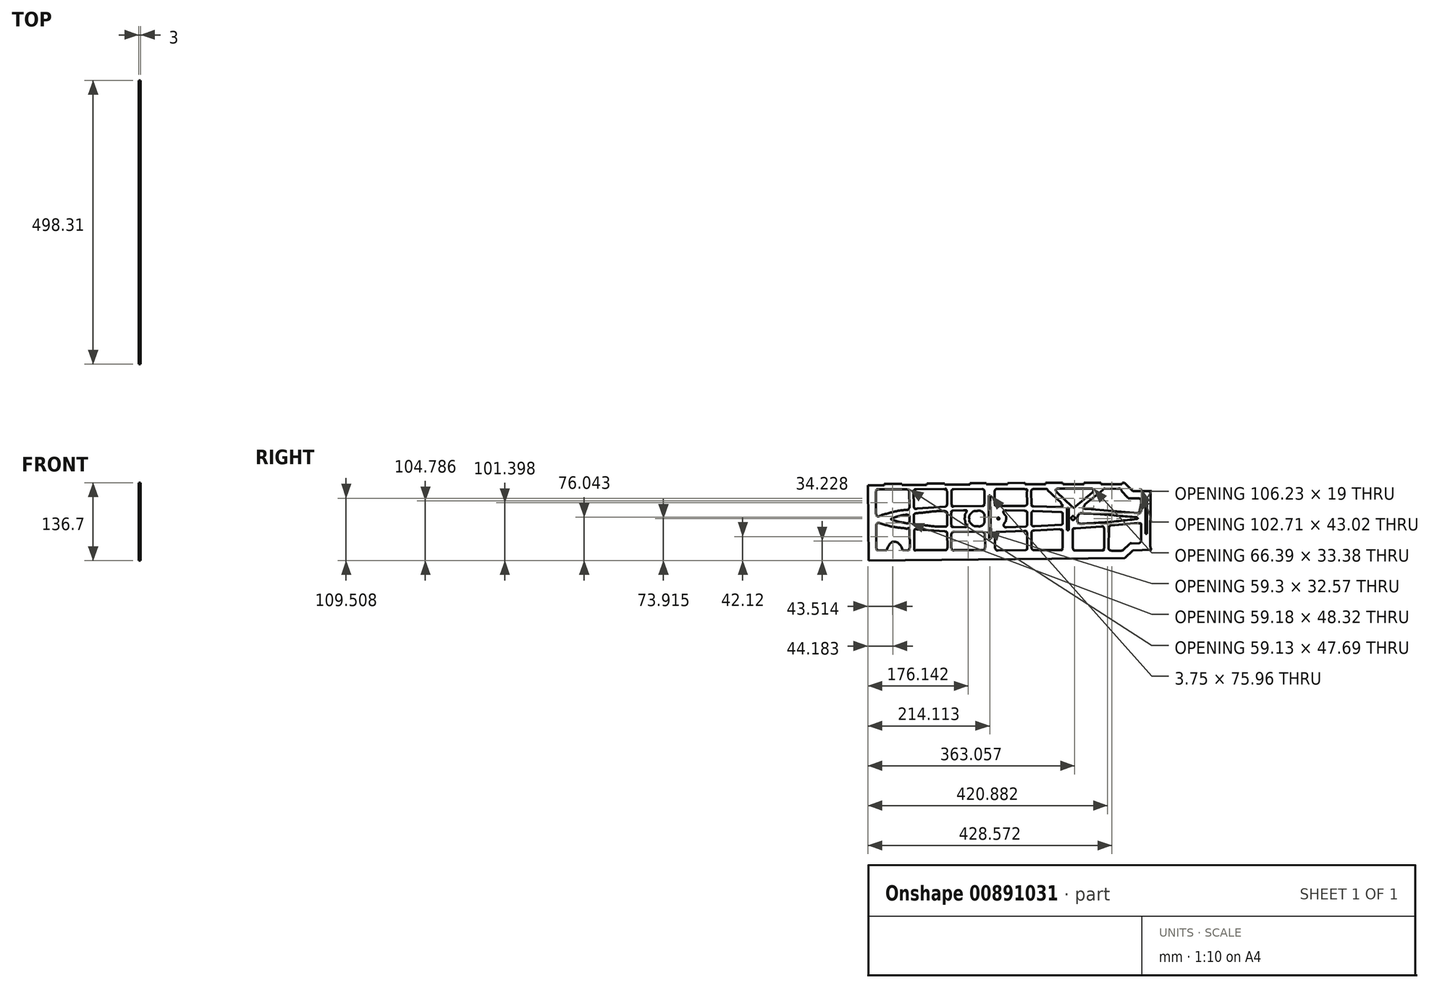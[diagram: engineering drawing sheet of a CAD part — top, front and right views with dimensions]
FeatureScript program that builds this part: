
annotation { "Feature Type Name" : "Feature", "Feature Type Description" : "" }
export const myFeature = defineFeature(function(context is Context, id is Id, definition is map)
    precondition{}
    {
        {
            var Q0;
            Q0=qCreatedBy(makeId("Right.planeOp"),FACE);
            var sketch = newSketch(context, id + "F0", { "sketchPlane" : qUnion([Q0])});
            skLineSegment(sketch, "E0", {"start": v(-252.36, 63.69) * mm, "end": v(-223.45, 63.69) * mm});
            skLineSegment(sketch, "E1", {"start": v(-223.45, 63.69) * mm, "end": v(-223.45, 66.35) * mm});
            skLineSegment(sketch, "E2", {"start": v(-223.45, 66.35) * mm, "end": v(-192.1, 66.21) * mm});
            skLineSegment(sketch, "E3", {"start": v(-192.1, 66.21) * mm, "end": v(-192.1, 64.1) * mm});
            skLineSegment(sketch, "E4", {"start": v(-192.1, 64.1) * mm, "end": v(-149.02, 64.53) * mm});
            skLineSegment(sketch, "E5", {"start": v(-149.02, 64.53) * mm, "end": v(-148.8, 66.91) * mm});
            skLineSegment(sketch, "E6", {"start": v(-148.8, 66.91) * mm, "end": v(-117.47, 67) * mm});
            skLineSegment(sketch, "E7", {"start": v(-117.47, 67) * mm, "end": v(-117.24, 64.87) * mm});
            skLineSegment(sketch, "E8", {"start": v(-117.24, 64.87) * mm, "end": v(-72.77, 65.07) * mm});
            skLineSegment(sketch, "E9", {"start": v(-72.77, 65.07) * mm, "end": v(-72.87, 67.27) * mm});
            skLineSegment(sketch, "E10", {"start": v(-72.87, 67.27) * mm, "end": v(-44.21, 67.47) * mm});
            skLineSegment(sketch, "E11", {"start": v(-44.21, 67.47) * mm, "end": v(-44.1, 65.43) * mm});
            skLineSegment(sketch, "E12", {"start": v(-44.1, 65.43) * mm, "end": v(-6.8, 65.66) * mm});
            skLineSegment(sketch, "E13", {"start": v(-6.8, 65.66) * mm, "end": v(-6.77, 67.67) * mm});
            skLineSegment(sketch, "E14", {"start": v(-6.77, 67.67) * mm, "end": v(23.4, 67.9) * mm});
            skLineSegment(sketch, "E15", {"start": v(23.4, 67.9) * mm, "end": v(23.47, 65.8) * mm});
            skLineSegment(sketch, "E16", {"start": v(23.47, 65.8) * mm, "end": v(59.52, 65.73) * mm});
            skLineSegment(sketch, "E17", {"start": v(59.52, 65.73) * mm, "end": v(59.8, 68.1) * mm});
            skLineSegment(sketch, "E18", {"start": v(59.8, 68.1) * mm, "end": v(89.83, 68.06) * mm});
            skLineSegment(sketch, "E19", {"start": v(89.83, 68.06) * mm, "end": v(90.13, 65.86) * mm});
            skLineSegment(sketch, "E20", {"start": v(90.13, 65.86) * mm, "end": v(126.94, 65.9) * mm});
            skLineSegment(sketch, "E21", {"start": v(126.94, 65.9) * mm, "end": v(126.8, 68.23) * mm});
            skLineSegment(sketch, "E22", {"start": v(126.8, 68.23) * mm, "end": v(156.97, 68.35) * mm});
            skLineSegment(sketch, "E23", {"start": v(156.97, 68.35) * mm, "end": v(157.08, 65.93) * mm});
            skLineSegment(sketch, "E24", {"start": v(157.08, 65.93) * mm, "end": v(193.78, 65.86) * mm});
            skLineSegment(sketch, "E25", {"start": v(193.78, 65.86) * mm, "end": v(194.06, 68.25) * mm});
            skLineSegment(sketch, "E26", {"start": v(194.06, 68.25) * mm, "end": v(198.27, 68.32) * mm});
            skLineSegment(sketch, "E27", {"start": v(198.27, 68.32) * mm, "end": v(212.86, 53.37) * mm});
            skLineSegment(sketch, "E28", {"start": v(212.86, 53.37) * mm, "end": v(252.36, 53.23) * mm});
            skLineSegment(sketch, "E29", {"start": v(243.66, 49.02) * mm, "end": v(243.52, -44.22) * mm});
            skLineSegment(sketch, "E30", {"start": v(250.68, -49) * mm, "end": v(212.95, -50.65) * mm});
            skLineSegment(sketch, "E31", {"start": v(212.95, -50.65) * mm, "end": v(198.74, -64.17) * mm});
            skLineSegment(sketch, "E32", {"start": v(198.74, -64.17) * mm, "end": v(-250.82, -68.35) * mm});
            skLineSegment(sketch, "E33", {"start": v(-250.82, -68.35) * mm, "end": v(-252.36, 63.69) * mm});
            skLineSegment(sketch, "E34", {"start": v(-234.1, 56.45) * mm, "end": v(-184.15, 56.9) * mm});
            skLineSegment(sketch, "E35", {"start": v(-179.86, 53.38) * mm, "end": v(-179.28, 24.52) * mm});
            skLineSegment(sketch, "E36", {"start": v(-237.93, 13.87) * mm, "end": v(-238.4, 52.2) * mm});
            skLineSegment(sketch, "E37", {"start": v(-166.84, 56.6) * mm, "end": v(-118.57, 57.23) * mm});
            skLineSegment(sketch, "E38", {"start": v(-113.3, 52.74) * mm, "end": v(-113.1, 30.64) * mm});
            skLineSegment(sketch, "E39", {"start": v(-116.53, 26.36) * mm, "end": v(-165.85, 22.78) * mm});
            skLineSegment(sketch, "E40", {"start": v(-171.68, 26.92) * mm, "end": v(-171.82, 52.95) * mm});
            skLineSegment(sketch, "E41", {"start": v(-101.8, 56.84) * mm, "end": v(-51.43, 57.37) * mm});
            skLineSegment(sketch, "E42", {"start": v(-47.85, 53.48) * mm, "end": v(-47.5, 32.96) * mm});
            skLineSegment(sketch, "E43", {"start": v(-51.44, 27.82) * mm, "end": v(-100.82, 27.06) * mm});
            skLineSegment(sketch, "E44", {"start": v(-105.59, 30.43) * mm, "end": v(-105.49, 53.35) * mm});
            skLineSegment(sketch, "E45", {"start": v(-179.21, 8.74) * mm, "end": v(-179.25, 0.2) * mm});
            skLineSegment(sketch, "E46", {"start": v(-206.6, 6.97) * mm, "end": v(-206.6, 6.97) * mm});
            skLineSegment(sketch, "E47", {"start": v(-178.97, -16.66) * mm, "end": v(-178.59, -45.67) * mm});
            skLineSegment(sketch, "E48", {"start": v(-181.9, -50.3) * mm, "end": v(-190.97, -50.13) * mm});
            skLineSegment(sketch, "E49", {"start": v(-219.62, -50.4) * mm, "end": v(-234.27, -50.26) * mm});
            skLineSegment(sketch, "E50", {"start": v(-237.35, -46.6) * mm, "end": v(-237.77, -6.6) * mm});
            skLineSegment(sketch, "E51", {"start": v(-113.1, 13.52) * mm, "end": v(-112.74, -4.65) * mm});
            skLineSegment(sketch, "E52", {"start": v(-171.26, -1.9) * mm, "end": v(-171.45, 10.26) * mm});
            skLineSegment(sketch, "E53", {"start": v(-103.04, 19.15) * mm, "end": v(-84.5, 19.9) * mm});
            skLineSegment(sketch, "E54", {"start": v(-80.9, -9.98) * mm, "end": v(-101.8, -9.35) * mm});
            skLineSegment(sketch, "E55", {"start": v(-105.7, -5.18) * mm, "end": v(-105.86, 15.1) * mm});
            skLineSegment(sketch, "E56", {"start": v(-165.01, -13.9) * mm, "end": v(-117.16, -17) * mm});
            skLineSegment(sketch, "E57", {"start": v(-112.88, -20.43) * mm, "end": v(-112.53, -45.34) * mm});
            skLineSegment(sketch, "E58", {"start": v(-116.88, -49.97) * mm, "end": v(-166.63, -49.97) * mm});
            skLineSegment(sketch, "E59", {"start": v(-170.9, -45.76) * mm, "end": v(-171.05, -18.47) * mm});
            skLineSegment(sketch, "E60", {"start": v(-101.1, -17.84) * mm, "end": v(-50.65, -18.33) * mm});
            skLineSegment(sketch, "E61", {"start": v(-46.7, -22.03) * mm, "end": v(-46.57, -44.97) * mm});
            skLineSegment(sketch, "E62", {"start": v(-50.85, -50.16) * mm, "end": v(-99.7, -49.83) * mm});
            skLineSegment(sketch, "E63", {"start": v(-105.87, -45.34) * mm, "end": v(-105.8, -22.96) * mm});
            skLineSegment(sketch, "E64", {"start": v(-40.12, 45.64) * mm, "end": v(-37.2, 45.67) * mm});
            skLineSegment(sketch, "E65", {"start": v(-37.2, 45.67) * mm, "end": v(-36.37, -30.25) * mm});
            skLineSegment(sketch, "E66", {"start": v(-36.37, -30.25) * mm, "end": v(-39.48, -30.29) * mm});
            skLineSegment(sketch, "E67", {"start": v(-39.48, -30.29) * mm, "end": v(-40.12, 45.64) * mm});
            skLineSegment(sketch, "E68", {"start": v(-26.2, 57.3) * mm, "end": v(22.51, 57.6) * mm});
            skLineSegment(sketch, "E69", {"start": v(26.98, 52.04) * mm, "end": v(27.03, 32.6) * mm});
            skLineSegment(sketch, "E70", {"start": v(23.1, 27.49) * mm, "end": v(-25.06, 27.79) * mm});
            skLineSegment(sketch, "E71", {"start": v(-29.72, 31.8) * mm, "end": v(-29.77, 53.53) * mm});
            skLineSegment(sketch, "E72", {"start": v(38.54, 57.45) * mm, "end": v(57.79, 57.6) * mm});
            skLineSegment(sketch, "E73", {"start": v(63.2, 55.32) * mm, "end": v(87.3, 32.94) * mm});
            skLineSegment(sketch, "E74", {"start": v(84.58, 25.45) * mm, "end": v(38.84, 26.64) * mm});
            skLineSegment(sketch, "E75", {"start": v(34.67, 30.12) * mm, "end": v(34.57, 53.04) * mm});
            skLineSegment(sketch, "E76", {"start": v(82.3, 57.75) * mm, "end": v(138.75, 57.85) * mm});
            skLineSegment(sketch, "E77", {"start": v(141.82, 51.15) * mm, "end": v(112.65, 27.1) * mm});
            skLineSegment(sketch, "E78", {"start": v(105.26, 27.1) * mm, "end": v(79.22, 51.45) * mm});
            skLineSegment(sketch, "E79", {"start": v(128.23, 30.12) * mm, "end": v(159.78, 55.32) * mm});
            skLineSegment(sketch, "E80", {"start": v(163.75, 57.7) * mm, "end": v(186.77, 57.6) * mm});
            skLineSegment(sketch, "E81", {"start": v(193.12, 53.73) * mm, "end": v(203.04, 42.62) * mm});
            skLineSegment(sketch, "E82", {"start": v(207.4, 40.95) * mm, "end": v(223.28, 40.93) * mm});
            skLineSegment(sketch, "E83", {"start": v(227.52, 36.7) * mm, "end": v(227.57, 18.53) * mm});
            skLineSegment(sketch, "E84", {"start": v(222.57, 15.05) * mm, "end": v(131.8, 22.28) * mm});
            skLineSegment(sketch, "E85", {"start": v(128.23, 30.12) * mm, "end": v(128.23, 30.12) * mm});
            skLineSegment(sketch, "E86", {"start": v(-9.68, 19.9) * mm, "end": v(22.07, 19.3) * mm});
            skLineSegment(sketch, "E87", {"start": v(27.26, 14.84) * mm, "end": v(27.52, -5.45) * mm});
            skLineSegment(sketch, "E88", {"start": v(24.1, -8.58) * mm, "end": v(-8.7, -9.67) * mm});
            skLineSegment(sketch, "E89", {"start": v(38.78, 18.7) * mm, "end": v(86.7, 16.9) * mm});
            skLineSegment(sketch, "E90", {"start": v(89.86, 13.25) * mm, "end": v(89.78, -2.61) * mm});
            skLineSegment(sketch, "E91", {"start": v(87.16, -5.5) * mm, "end": v(40.52, -8.08) * mm});
            skLineSegment(sketch, "E92", {"start": v(34.77, -4.11) * mm, "end": v(34.78, 15.5) * mm});
            skLineSegment(sketch, "E93", {"start": v(-25.66, -17.89) * mm, "end": v(22.46, -16.42) * mm});
            skLineSegment(sketch, "E94", {"start": v(27.36, -21.03) * mm, "end": v(27.5, -46.52) * mm});
            skLineSegment(sketch, "E95", {"start": v(24.57, -49.81) * mm, "end": v(-23.77, -50.55) * mm});
            skLineSegment(sketch, "E96", {"start": v(-29.02, -46.27) * mm, "end": v(-29.07, -21.47) * mm});
            skLineSegment(sketch, "E97", {"start": v(39.79, -15.66) * mm, "end": v(84.58, -13.44) * mm});
            skLineSegment(sketch, "E98", {"start": v(89.72, -18.03) * mm, "end": v(89.52, -46.06) * mm});
            skLineSegment(sketch, "E99", {"start": v(84.97, -50.15) * mm, "end": v(38.36, -50.1) * mm});
            skLineSegment(sketch, "E100", {"start": v(35.16, -46.98) * mm, "end": v(35, -19.27) * mm});
            skLineSegment(sketch, "E101", {"start": v(97.42, 23.69) * mm, "end": v(100.18, 23.83) * mm});
            skLineSegment(sketch, "E102", {"start": v(100.18, 23.83) * mm, "end": v(100.25, -15.23) * mm});
            skLineSegment(sketch, "E103", {"start": v(100.25, -15.23) * mm, "end": v(97.28, -15.23) * mm});
            skLineSegment(sketch, "E104", {"start": v(97.28, -15.23) * mm, "end": v(97.42, 23.69) * mm});
            skLineSegment(sketch, "E105", {"start": v(112.36, -11.65) * mm, "end": v(157, -8.68) * mm});
            skLineSegment(sketch, "E106", {"start": v(162.6, -12.73) * mm, "end": v(162.76, -46.38) * mm});
            skLineSegment(sketch, "E107", {"start": v(157.6, -50.55) * mm, "end": v(111.56, -50.35) * mm});
            skLineSegment(sketch, "E108", {"start": v(107.6, -46.78) * mm, "end": v(107.4, -16.61) * mm});
            skLineSegment(sketch, "E109", {"start": v(173.9, -6.97) * mm, "end": v(222.1, -2.53) * mm});
            skLineSegment(sketch, "E110", {"start": v(227.29, -6.42) * mm, "end": v(227.58, -33.56) * mm});
            skLineSegment(sketch, "E111", {"start": v(223.88, -37.65) * mm, "end": v(210.19, -38.24) * mm});
            skLineSegment(sketch, "E112", {"start": v(206.28, -39.57) * mm, "end": v(196.1, -49.36) * mm});
            skLineSegment(sketch, "E113", {"start": v(193.06, -50.94) * mm, "end": v(175.06, -50.94) * mm});
            skLineSegment(sketch, "E114", {"start": v(170.2, -46.27) * mm, "end": v(170.57, -10.88) * mm});
            skLineSegment(sketch, "E115", {"start": v(235.1, 35.08) * mm, "end": v(237.37, 35.08) * mm});
            skLineSegment(sketch, "E116", {"start": v(237.37, 35.08) * mm, "end": v(237.63, -21.28) * mm});
            skLineSegment(sketch, "E117", {"start": v(237.63, -21.28) * mm, "end": v(235.19, -21.2) * mm});
            skLineSegment(sketch, "E118", {"start": v(235.19, -21.2) * mm, "end": v(235.1, 35.08) * mm});
            skFitSpline(sketch, "E119", {"points": [v(252.36, 53.23) * mm, v(247.1, 53.4) * mm, v(243.87, 52.22) * mm, v(243.66, 49.02) * mm]});
            skFitSpline(sketch, "E120", {"points": [v(243.52, -44.22) * mm, v(244.45, -47.17) * mm, v(246.08, -49.46) * mm, v(250.68, -49) * mm]});
            skFitSpline(sketch, "E121", {"points": [v(-238.4, 52.2) * mm, v(-237.5, 54.07) * mm, v(-237.03, 56.33) * mm, v(-234.1, 56.45) * mm]});
            skFitSpline(sketch, "E122", {"points": [v(-184.15, 56.9) * mm, v(-182.24, 56.2) * mm, v(-180, 55.84) * mm, v(-179.86, 53.38) * mm]});
            skFitSpline(sketch, "E123", {"points": [v(-179.28, 24.52) * mm, v(-180.73, 22) * mm, v(-181.94, 20.66) * mm, v(-182.86, 20.8) * mm]});
            skFitSpline(sketch, "E124", {"points": [v(-182.86, 20.8) * mm, v(-197.64, 19.17) * mm, v(-212.62, 15.7) * mm, v(-227.66, 11.71) * mm]});
            skFitSpline(sketch, "E125", {"points": [v(-227.66, 11.71) * mm, v(-231.86, 9.78) * mm, v(-235.59, 9.44) * mm, v(-237.93, 13.87) * mm]});
            skFitSpline(sketch, "E126", {"points": [v(-171.82, 52.95) * mm, v(-171.09, 55.03) * mm, v(-169.97, 56.74) * mm, v(-166.84, 56.6) * mm]});
            skFitSpline(sketch, "E127", {"points": [v(-118.57, 57.23) * mm, v(-116.95, 56.52) * mm, v(-115.77, 58.23) * mm, v(-113.3, 52.74) * mm]});
            skFitSpline(sketch, "E128", {"points": [v(-113.1, 30.64) * mm, v(-113.54, 29.27) * mm, v(-113.74, 27.91) * mm, v(-116.53, 26.36) * mm]});
            skFitSpline(sketch, "E129", {"points": [v(-165.85, 22.78) * mm, v(-169.57, 22.4) * mm, v(-170.93, 24.35) * mm, v(-171.68, 26.92) * mm]});
            skFitSpline(sketch, "E130", {"points": [v(-105.49, 53.35) * mm, v(-104.72, 55.44) * mm, v(-103.62, 56.86) * mm, v(-101.8, 56.84) * mm]});
            skFitSpline(sketch, "E131", {"points": [v(-51.43, 57.37) * mm, v(-49.65, 56.58) * mm, v(-48.23, 55.48) * mm, v(-47.85, 53.48) * mm]});
            skFitSpline(sketch, "E132", {"points": [v(-47.5, 32.96) * mm, v(-47.94, 30.63) * mm, v(-48.42, 28.1) * mm, v(-51.44, 27.82) * mm]});
            skFitSpline(sketch, "E133", {"points": [v(-100.82, 27.06) * mm, v(-104.61, 26.58) * mm, v(-104.46, 28.97) * mm, v(-105.59, 30.43) * mm]});
            skFitSpline(sketch, "E134", {"points": [v(-206.6, 6.97) * mm, v(-198.88, 9.42) * mm, v(-191.29, 11.24) * mm, v(-183.83, 12.36) * mm]});
            skFitSpline(sketch, "E135", {"points": [v(-183.83, 12.36) * mm, v(-181.73, 11.67) * mm, v(-179.75, 10.86) * mm, v(-179.21, 8.74) * mm]});
            skFitSpline(sketch, "E136", {"points": [v(-179.25, 0.2) * mm, v(-179.77, -1.53) * mm, v(-180.96, -2.7) * mm, v(-183.07, -3.11) * mm]});
            skFitSpline(sketch, "E137", {"points": [v(-183.07, -3.11) * mm, v(-191, -1.72) * mm, v(-198.89, -0.22) * mm, v(-206.55, 2.22) * mm]});
            skFitSpline(sketch, "E138", {"points": [v(-206.55, 2.22) * mm, v(-211.7, 4.5) * mm, v(-208.32, 6.06) * mm, v(-206.6, 6.97) * mm]});
            skFitSpline(sketch, "E139", {"points": [v(-237.77, -6.6) * mm, v(-236.87, -4.17) * mm, v(-234.94, -2.22) * mm, v(-230.37, -2.67) * mm]});
            skFitSpline(sketch, "E140", {"points": [v(-230.37, -2.67) * mm, v(-215.68, -7.3) * mm, v(-200.68, -10.2) * mm, v(-185.47, -11.93) * mm]});
            skFitSpline(sketch, "E141", {"points": [v(-185.47, -11.93) * mm, v(-183.19, -12.71) * mm, v(-180.52, -10.82) * mm, v(-178.97, -16.66) * mm]});
            skFitSpline(sketch, "E142", {"points": [v(-178.59, -45.67) * mm, v(-179.37, -47.54) * mm, v(-180.1, -49.45) * mm, v(-181.9, -50.3) * mm]});
            skFitSpline(sketch, "E143", {"points": [v(-190.97, -50.13) * mm, v(-197.72, -38.52) * mm, v(-209.37, -35.61) * mm, v(-219.62, -50.4) * mm]});
            skFitSpline(sketch, "E144", {"points": [v(-234.27, -50.26) * mm, v(-236.58, -49.77) * mm, v(-236.81, -48.1) * mm, v(-237.35, -46.6) * mm]});
            skFitSpline(sketch, "E145", {"points": [v(-171.45, 10.26) * mm, v(-170.77, 13.41) * mm, v(-168.93, 14.35) * mm, v(-166.8, 14.75) * mm]});
            skFitSpline(sketch, "E146", {"points": [v(-166.8, 14.75) * mm, v(-150.4, 16.4) * mm, v(-133.93, 18.2) * mm, v(-118.08, 18.57) * mm]});
            skFitSpline(sketch, "E147", {"points": [v(-118.08, 18.57) * mm, v(-115.71, 18.02) * mm, v(-113.61, 17.04) * mm, v(-113.1, 13.52) * mm]});
            skFitSpline(sketch, "E148", {"points": [v(-112.74, -4.65) * mm, v(-113.14, -6.59) * mm, v(-114.1, -8.2) * mm, v(-117.02, -8.79) * mm]});
            skFitSpline(sketch, "E149", {"points": [v(-117.02, -8.79) * mm, v(-133.43, -8.43) * mm, v(-149.84, -6.76) * mm, v(-166.26, -5.11) * mm]});
            skFitSpline(sketch, "E150", {"points": [v(-166.26, -5.11) * mm, v(-169.18, -5.15) * mm, v(-170.57, -3.84) * mm, v(-171.26, -1.9) * mm]});
            skFitSpline(sketch, "E151", {"points": [v(-84.5, 19.9) * mm, v(-81.84, 19.72) * mm, v(-79.04, 19.9) * mm, v(-79.73, 15.35) * mm]});
            skFitSpline(sketch, "E152", {"points": [v(-79.73, 15.35) * mm, v(-81.85, 12.37) * mm, v(-81.99, 8.51) * mm, v(-82.5, 4.82) * mm]});
            skFitSpline(sketch, "E153", {"points": [v(-82.5, 4.82) * mm, v(-81.55, 1.42) * mm, v(-80.92, -2.72) * mm, v(-79.28, -4.58) * mm]});
            skFitSpline(sketch, "E154", {"points": [v(-79.28, -4.58) * mm, v(-79.14, -6.2) * mm, v(-77.2, -7.34) * mm, v(-80.9, -9.98) * mm]});
            skFitSpline(sketch, "E155", {"points": [v(-101.8, -9.35) * mm, v(-105.39, -8.77) * mm, v(-105.12, -6.82) * mm, v(-105.7, -5.18) * mm]});
            skFitSpline(sketch, "E156", {"points": [v(-105.86, 15.1) * mm, v(-105.56, 16.6) * mm, v(-105.67, 18.2) * mm, v(-103.04, 19.15) * mm]});
            skFitSpline(sketch, "E157", {"points": [v(-171.05, -18.47) * mm, v(-170.6, -15.15) * mm, v(-169.18, -12.94) * mm, v(-165.01, -13.9) * mm]});
            skFitSpline(sketch, "E158", {"points": [v(-117.16, -17) * mm, v(-115.7, -17.65) * mm, v(-114.18, -17.66) * mm, v(-112.88, -20.43) * mm]});
            skFitSpline(sketch, "E159", {"points": [v(-112.53, -45.34) * mm, v(-113.12, -47.83) * mm, v(-114.25, -49.71) * mm, v(-116.88, -49.97) * mm]});
            skFitSpline(sketch, "E160", {"points": [v(-166.63, -49.97) * mm, v(-170.63, -50.11) * mm, v(-170.5, -47.77) * mm, v(-170.9, -45.76) * mm]});
            skFitSpline(sketch, "E161", {"points": [v(-105.8, -22.96) * mm, v(-105.4, -20.67) * mm, v(-103.73, -18.63) * mm, v(-101.1, -17.84) * mm]});
            skFitSpline(sketch, "E162", {"points": [v(-50.65, -18.33) * mm, v(-48.9, -19.02) * mm, v(-47.07, -19.95) * mm, v(-46.7, -22.03) * mm]});
            skFitSpline(sketch, "E163", {"points": [v(-46.57, -44.97) * mm, v(-46.8, -46.93) * mm, v(-47.24, -48.85) * mm, v(-50.85, -50.16) * mm]});
            skFitSpline(sketch, "E164", {"points": [v(-99.7, -49.83) * mm, v(-102.24, -50.41) * mm, v(-104.38, -49.25) * mm, v(-105.87, -45.34) * mm]});
            skFitSpline(sketch, "E165", {"points": [v(-29.77, 53.53) * mm, v(-29.04, 54.94) * mm, v(-28.47, 56.4) * mm, v(-26.2, 57.3) * mm]});
            skFitSpline(sketch, "E166", {"points": [v(22.51, 57.6) * mm, v(24.3, 56.41) * mm, v(26.9, 57) * mm, v(26.98, 52.04) * mm]});
            skFitSpline(sketch, "E167", {"points": [v(27.03, 32.6) * mm, v(27.08, 30) * mm, v(25.43, 28.51) * mm, v(23.1, 27.49) * mm]});
            skFitSpline(sketch, "E168", {"points": [v(-25.06, 27.79) * mm, v(-29.4, 28.83) * mm, v(-28.78, 30.4) * mm, v(-29.72, 31.8) * mm]});
            skFitSpline(sketch, "E169", {"points": [v(34.57, 53.04) * mm, v(34.98, 55.56) * mm, v(36.55, 56.76) * mm, v(38.54, 57.45) * mm]});
            skFitSpline(sketch, "E170", {"points": [v(57.79, 57.6) * mm, v(59.85, 57.4) * mm, v(62.02, 57.43) * mm, v(63.2, 55.32) * mm]});
            skFitSpline(sketch, "E171", {"points": [v(87.3, 32.94) * mm, v(87.73, 30.48) * mm, v(89.99, 28.05) * mm, v(84.58, 25.45) * mm]});
            skFitSpline(sketch, "E172", {"points": [v(38.84, 26.64) * mm, v(35.14, 27.71) * mm, v(35.83, 28.99) * mm, v(34.67, 30.12) * mm]});
            skFitSpline(sketch, "E173", {"points": [v(79.22, 51.45) * mm, v(77.7, 54.62) * mm, v(77.88, 57.08) * mm, v(82.3, 57.75) * mm]});
            skFitSpline(sketch, "E174", {"points": [v(138.75, 57.85) * mm, v(142.1, 57.55) * mm, v(143.87, 55.93) * mm, v(141.82, 51.15) * mm]});
            skFitSpline(sketch, "E175", {"points": [v(112.65, 27.1) * mm, v(109.4, 24.43) * mm, v(107.2, 25.28) * mm, v(105.26, 27.1) * mm]});
            skFitSpline(sketch, "E176", {"points": [v(159.78, 55.32) * mm, v(160.76, 56.46) * mm, v(161.74, 57.6) * mm, v(163.75, 57.7) * mm]});
            skFitSpline(sketch, "E177", {"points": [v(186.77, 57.6) * mm, v(190.12, 57.84) * mm, v(192.14, 56.3) * mm, v(193.12, 53.73) * mm]});
            skFitSpline(sketch, "E178", {"points": [v(203.04, 42.62) * mm, v(204.26, 41.9) * mm, v(205.06, 40.89) * mm, v(207.4, 40.95) * mm]});
            skFitSpline(sketch, "E179", {"points": [v(223.28, 40.93) * mm, v(225.15, 40.18) * mm, v(226.94, 39.3) * mm, v(227.52, 36.7) * mm]});
            skFitSpline(sketch, "E180", {"points": [v(227.57, 18.53) * mm, v(226.49, 16.79) * mm, v(225.3, 15.14) * mm, v(222.57, 15.05) * mm]});
            skFitSpline(sketch, "E181", {"points": [v(131.8, 22.28) * mm, v(124.74, 24.13) * mm, v(127.55, 27.26) * mm, v(128.23, 30.12) * mm]});
            skFitSpline(sketch, "E182", {"points": [v(-13.45, 13.94) * mm, v(-14.25, 16.07) * mm, v(-14.42, 18.14) * mm, v(-9.68, 19.9) * mm]});
            skFitSpline(sketch, "E183", {"points": [v(22.07, 19.3) * mm, v(24.59, 18.75) * mm, v(26.78, 17.8) * mm, v(27.26, 14.84) * mm]});
            skFitSpline(sketch, "E184", {"points": [v(27.52, -5.45) * mm, v(26.84, -7.09) * mm, v(25.7, -8.14) * mm, v(24.1, -8.58) * mm]});
            skFitSpline(sketch, "E185", {"points": [v(-8.7, -9.67) * mm, v(-11.91, -9.47) * mm, v(-13.93, -6.57) * mm, v(-13.1, -3.72) * mm]});
            skFitSpline(sketch, "E186", {"points": [v(-13.1, -3.72) * mm, v(-11.3, -0.55) * mm, v(-10.18, 0.8) * mm, v(-9.68, 4.62) * mm]});
            skFitSpline(sketch, "E187", {"points": [v(-9.68, 4.62) * mm, v(-9.54, 8.9) * mm, v(-11.39, 11.5) * mm, v(-13.45, 13.94) * mm]});
            skFitSpline(sketch, "E188", {"points": [v(34.78, 15.5) * mm, v(35.62, 17.15) * mm, v(36.83, 18.36) * mm, v(38.78, 18.7) * mm]});
            skFitSpline(sketch, "E189", {"points": [v(86.7, 16.9) * mm, v(88.46, 16.13) * mm, v(89.6, 14.96) * mm, v(89.86, 13.25) * mm]});
            skFitSpline(sketch, "E190", {"points": [v(89.78, -2.61) * mm, v(89.22, -4.31) * mm, v(88.27, -5.1) * mm, v(87.16, -5.5) * mm]});
            skFitSpline(sketch, "E191", {"points": [v(40.52, -8.08) * mm, v(37.3, -7.88) * mm, v(35.37, -6.56) * mm, v(34.77, -4.11) * mm]});
            skFitSpline(sketch, "E192", {"points": [v(-29.07, -21.47) * mm, v(-28.4, -20.1) * mm, v(-27.79, -18.71) * mm, v(-25.66, -17.89) * mm]});
            skFitSpline(sketch, "E193", {"points": [v(22.46, -16.42) * mm, v(25.73, -16.53) * mm, v(26.88, -18.5) * mm, v(27.36, -21.03) * mm]});
            skFitSpline(sketch, "E194", {"points": [v(27.5, -46.52) * mm, v(27.2, -48.51) * mm, v(25.99, -49.3) * mm, v(24.57, -49.81) * mm]});
            skFitSpline(sketch, "E195", {"points": [v(-23.77, -50.55) * mm, v(-26.98, -50.1) * mm, v(-28.01, -48.2) * mm, v(-29.02, -46.27) * mm]});
            skFitSpline(sketch, "E196", {"points": [v(35, -19.27) * mm, v(35.93, -16.64) * mm, v(37.73, -15.88) * mm, v(39.79, -15.66) * mm]});
            skFitSpline(sketch, "E197", {"points": [v(84.58, -13.44) * mm, v(86.45, -14.19) * mm, v(88.55, -13.77) * mm, v(89.72, -18.03) * mm]});
            skFitSpline(sketch, "E198", {"points": [v(89.52, -46.06) * mm, v(88.8, -47.72) * mm, v(88.81, -49.65) * mm, v(84.97, -50.15) * mm]});
            skFitSpline(sketch, "E199", {"points": [v(38.36, -50.1) * mm, v(37.3, -49.51) * mm, v(36.23, -48.67) * mm, v(35.16, -46.98) * mm]});
            skFitSpline(sketch, "E200", {"points": [v(127.36, 14.45) * mm, v(158.19, 12.8) * mm, v(188.81, 10.13) * mm, v(219.47, 7.6) * mm]});
            skFitSpline(sketch, "E201", {"points": [v(219.47, 7.6) * mm, v(220.6, 6.66) * mm, v(221.65, 5.73) * mm, v(219.31, 4.62) * mm]});
            skFitSpline(sketch, "E202", {"points": [v(219.31, 4.62) * mm, v(189, 1.17) * mm, v(158.67, -1.55) * mm, v(128.35, -3.32) * mm]});
            skFitSpline(sketch, "E203", {"points": [v(128.35, -3.32) * mm, v(116.62, -1.68) * mm, v(118.36, 13.34) * mm, v(127.36, 14.45) * mm]});
            skFitSpline(sketch, "E204", {"points": [v(107.4, -16.61) * mm, v(107.34, -13.97) * mm, v(108.34, -11.93) * mm, v(112.36, -11.65) * mm]});
            skFitSpline(sketch, "E205", {"points": [v(157, -8.68) * mm, v(161.07, -8.68) * mm, v(161.82, -10.71) * mm, v(162.6, -12.73) * mm]});
            skFitSpline(sketch, "E206", {"points": [v(162.76, -46.38) * mm, v(161.66, -48.16) * mm, v(161.5, -50.52) * mm, v(157.6, -50.55) * mm]});
            skFitSpline(sketch, "E207", {"points": [v(111.56, -50.35) * mm, v(109.14, -50.26) * mm, v(108.27, -48.61) * mm, v(107.6, -46.78) * mm]});
            skFitSpline(sketch, "E208", {"points": [v(170.57, -10.88) * mm, v(170.62, -8.51) * mm, v(172.44, -7.92) * mm, v(173.9, -6.97) * mm]});
            skFitSpline(sketch, "E209", {"points": [v(222.1, -2.53) * mm, v(224.57, -2.89) * mm, v(227, -3.32) * mm, v(227.29, -6.42) * mm]});
            skFitSpline(sketch, "E210", {"points": [v(227.58, -33.56) * mm, v(226.8, -35.57) * mm, v(225.59, -36.95) * mm, v(223.88, -37.65) * mm]});
            skFitSpline(sketch, "E211", {"points": [v(210.19, -38.24) * mm, v(208.76, -37.95) * mm, v(207.52, -38.77) * mm, v(206.28, -39.57) * mm]});
            skFitSpline(sketch, "E212", {"points": [v(196.1, -49.36) * mm, v(195.49, -50.55) * mm, v(194.2, -50.63) * mm, v(193.06, -50.94) * mm]});
            skFitSpline(sketch, "E213", {"points": [v(175.06, -50.94) * mm, v(172.52, -50.31) * mm, v(170.88, -48.78) * mm, v(170.2, -46.27) * mm]});
            skFitSpline(sketch, "E214", {"points": [v(-47.84, 5.43) * mm, v(-47.84, -1.93) * mm, v(-53.8, -7.9) * mm, v(-61.16, -7.9) * mm]});
            skFitSpline(sketch, "E215", {"points": [v(-61.16, -7.9) * mm, v(-64.7, -7.9) * mm, v(-68.08, -6.49) * mm, v(-70.58, -4) * mm]});
            skFitSpline(sketch, "E216", {"points": [v(-70.58, -4) * mm, v(-73.08, -1.5) * mm, v(-74.48, 1.9) * mm, v(-74.48, 5.43) * mm]});
            skFitSpline(sketch, "E217", {"points": [v(-74.48, 5.43) * mm, v(-74.48, 8.96) * mm, v(-73.08, 12.35) * mm, v(-70.58, 14.85) * mm]});
            skFitSpline(sketch, "E218", {"points": [v(-70.58, 14.85) * mm, v(-68.08, 17.35) * mm, v(-64.7, 18.75) * mm, v(-61.16, 18.75) * mm]});
            skFitSpline(sketch, "E219", {"points": [v(-61.16, 18.75) * mm, v(-53.8, 18.75) * mm, v(-47.84, 12.79) * mm, v(-47.84, 5.43) * mm]});
            skFitSpline(sketch, "E220", {"points": [v(-21.4, 5.46) * mm, v(-21.4, 5) * mm, v(-21.58, 4.56) * mm, v(-21.9, 4.24) * mm]});
            skFitSpline(sketch, "E221", {"points": [v(-21.9, 4.24) * mm, v(-22.23, 3.91) * mm, v(-22.67, 3.73) * mm, v(-23.13, 3.73) * mm]});
            skFitSpline(sketch, "E222", {"points": [v(-23.13, 3.73) * mm, v(-23.59, 3.73) * mm, v(-24.03, 3.91) * mm, v(-24.35, 4.24) * mm]});
            skFitSpline(sketch, "E223", {"points": [v(-24.35, 4.24) * mm, v(-24.68, 4.56) * mm, v(-24.86, 5) * mm, v(-24.86, 5.46) * mm]});
            skFitSpline(sketch, "E224", {"points": [v(-24.86, 5.46) * mm, v(-24.86, 5.92) * mm, v(-24.68, 6.36) * mm, v(-24.35, 6.69) * mm]});
            skFitSpline(sketch, "E225", {"points": [v(-24.35, 6.69) * mm, v(-24.03, 7.01) * mm, v(-23.59, 7.2) * mm, v(-23.13, 7.2) * mm]});
            skFitSpline(sketch, "E226", {"points": [v(-23.13, 7.2) * mm, v(-22.67, 7.2) * mm, v(-22.23, 7.01) * mm, v(-21.9, 6.69) * mm]});
            skFitSpline(sketch, "E227", {"points": [v(-21.9, 6.69) * mm, v(-21.58, 6.36) * mm, v(-21.4, 5.92) * mm, v(-21.4, 5.46) * mm]});
            skFitSpline(sketch, "E228", {"points": [v(111.02, 6.22) * mm, v(111.02, 5.37) * mm, v(110.68, 4.55) * mm, v(110.08, 3.95) * mm]});
            skFitSpline(sketch, "E229", {"points": [v(110.08, 3.95) * mm, v(109.47, 3.34) * mm, v(108.66, 3) * mm, v(107.8, 3) * mm]});
            skFitSpline(sketch, "E230", {"points": [v(107.8, 3) * mm, v(106.95, 3) * mm, v(106.14, 3.34) * mm, v(105.53, 3.95) * mm]});
            skFitSpline(sketch, "E231", {"points": [v(105.53, 3.95) * mm, v(104.93, 4.55) * mm, v(104.6, 5.37) * mm, v(104.6, 6.22) * mm]});
            skFitSpline(sketch, "E232", {"points": [v(104.6, 6.22) * mm, v(104.6, 7.07) * mm, v(104.93, 7.89) * mm, v(105.53, 8.49) * mm]});
            skFitSpline(sketch, "E233", {"points": [v(105.53, 8.49) * mm, v(106.14, 9.1) * mm, v(106.95, 9.43) * mm, v(107.8, 9.43) * mm]});
            skFitSpline(sketch, "E234", {"points": [v(107.8, 9.43) * mm, v(108.66, 9.43) * mm, v(109.47, 9.1) * mm, v(110.08, 8.49) * mm]});
            skFitSpline(sketch, "E235", {"points": [v(110.08, 8.49) * mm, v(110.68, 7.89) * mm, v(111.02, 7.07) * mm, v(111.02, 6.22) * mm]});
            skSolve(sketch);
        }
        {
            var Q0;
            Q0=makeQuery(id+"F0.imprint","IMPRINT",FACE,{"disambiguationData":[TD([[makeQuery(id+"F0.imprint","IMPRINT",EDGE,{"derivedFrom":sQuery(id+"F0.wireOp",EDGE,"E0")}),-1.0]])]});
            extrude(context, id + "F1", {"entities" : qUnion([Q0]), "depth" : 3 * mm, "offsetDistance" : 25 * mm});
        }
    });
